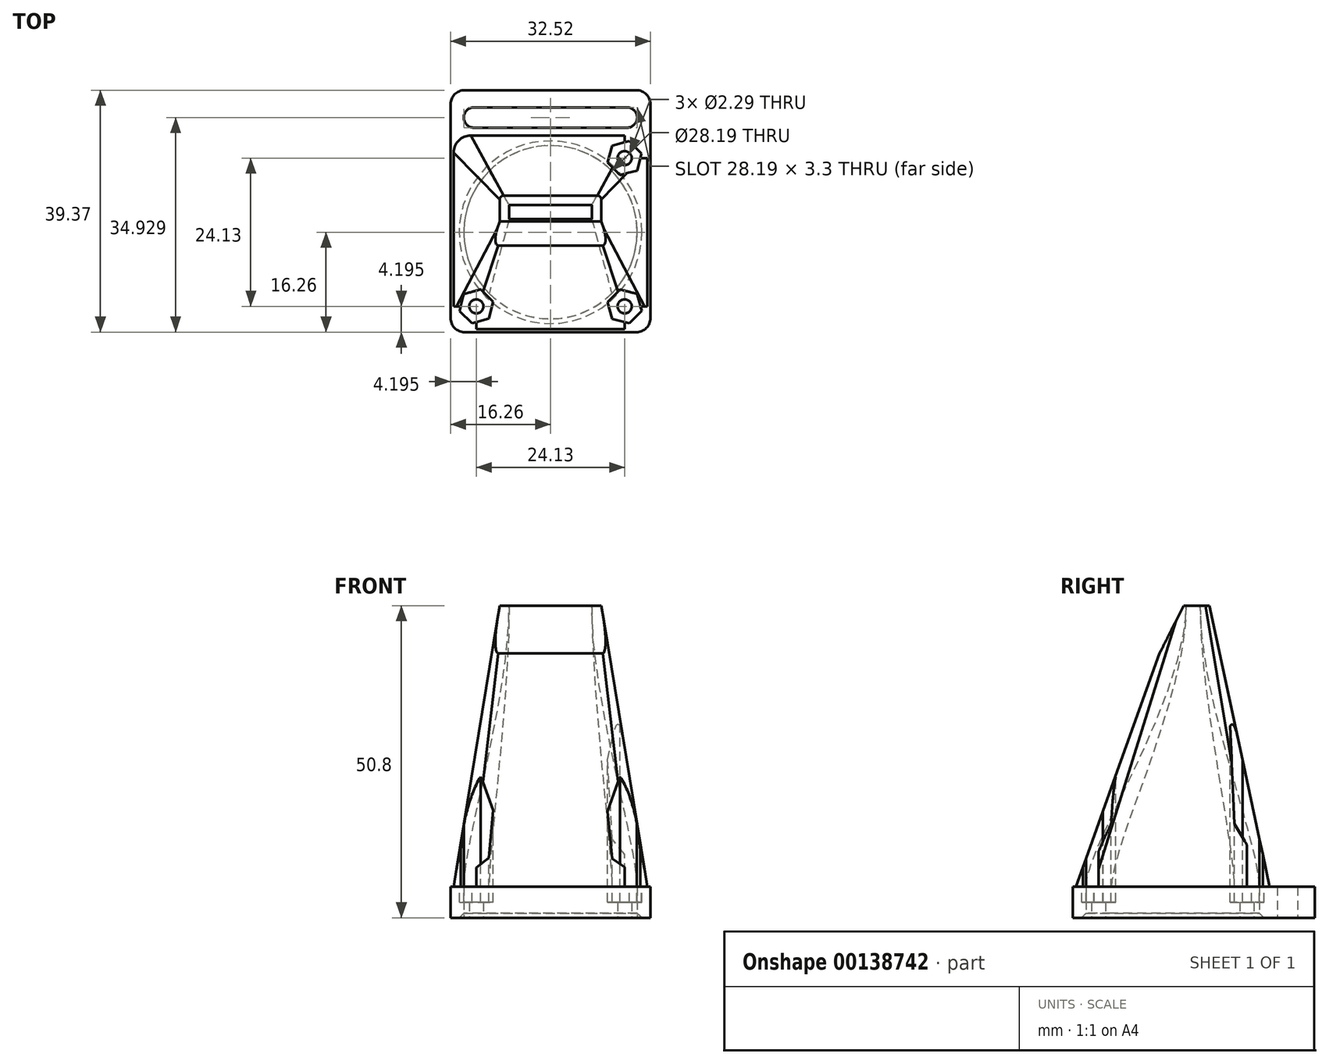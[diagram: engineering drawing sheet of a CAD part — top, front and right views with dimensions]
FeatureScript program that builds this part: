
annotation { "Feature Type Name" : "Feature", "Feature Type Description" : "" }
export const myFeature = defineFeature(function(context is Context, id is Id, definition is map)
    precondition{}
    {
        {
            var Q0;
            Q0=qCreatedBy(makeId("Top.planeOp"),FACE);
            var sketch = newSketch(context, id + "F0", { "sketchPlane" : qUnion([Q0])});
            skCircle(sketch, "E0", {"center": v(0, 0) * mm, "radius": 14.1 * mm});
            skLineSegment(sketch, "E1.top", {"start": v(-13.97, -16.26) * mm, "end": v(13.97, -16.26) * mm});
            skLineSegment(sketch, "E1.left", {"start": v(-16.26, 20.83) * mm, "end": v(-16.26, -13.97) * mm});
            skLineSegment(sketch, "E1.right", {"start": v(16.26, 20.83) * mm, "end": v(16.26, -13.97) * mm});
            skCircle(sketch, "E2", {"center": v(12.07, -12.07) * mm, "radius": 1.14 * mm});
            skCircle(sketch, "E3", {"center": v(-12.07, -12.07) * mm, "radius": 1.14 * mm});
            skCircle(sketch, "E4", {"center": v(12.07, 12.06) * mm, "radius": 1.14 * mm});
            skPoint(sketch, "E5.visualSharp", {"position": v(16.26, -16.26) * mm});
            skArc(sketch, "E5.filletArc", {"start": v(13.97, -16.26) * mm, "mid": v(15.59, -15.59) * mm, "end": v(16.26, -13.97) * mm});
            skPoint(sketch, "E6.visualSharp", {"position": v(-16.26, -16.26) * mm});
            skArc(sketch, "E6.filletArc", {"start": v(-16.26, -13.97) * mm, "mid": v(-15.59, -15.59) * mm, "end": v(-13.97, -16.26) * mm});
            skLineSegment(sketch, "E7.top", {"start": v(-13.97, 23.11) * mm, "end": v(13.97, 23.11) * mm});
            skArc(sketch, "E8", {"start": v(12.45, 17.02) * mm, "mid": v(14.1, 18.67) * mm, "end": v(12.45, 20.32) * mm});
            skArc(sketch, "E9", {"start": v(-12.45, 20.32) * mm, "mid": v(-14.1, 18.67) * mm, "end": v(-12.45, 17.02) * mm});
            skLineSegment(sketch, "E10", {"start": v(-12.45, 20.32) * mm, "end": v(12.45, 20.32) * mm});
            skLineSegment(sketch, "E11", {"start": v(12.45, 17.02) * mm, "end": v(-12.45, 17.02) * mm});
            skPoint(sketch, "E12.visualSharp", {"position": v(16.26, 23.11) * mm});
            skArc(sketch, "E12.filletArc", {"start": v(16.26, 20.83) * mm, "mid": v(15.59, 22.44) * mm, "end": v(13.97, 23.11) * mm});
            skPoint(sketch, "E13.visualSharp", {"position": v(-16.26, 23.11) * mm});
            skArc(sketch, "E13.filletArc", {"start": v(-13.97, 23.11) * mm, "mid": v(-15.59, 22.44) * mm, "end": v(-16.26, 20.83) * mm});
            skSolve(sketch);
        }
        {
            var Q0;
            Q0=qSketchRegion(id+"F0",true);
            extrude(context, id + "F1", {"entities" : qUnion([Q0]), "depth" : 5.08 * mm});
        }
        {
            var Q0;
            Q0=qCreatedBy(makeId("Top.planeOp"),FACE);
            cPlane(context, id + "F2", {"entities" : qUnion([Q0]), "cplaneType" : CPlaneType.OFFSET, "offset" : 50.8 * mm, "width" : 152.4 * mm, "height" : 152.4 * mm});
        }
        {
            var Q0;
            Q0=qCreatedBy(id+"F2.planeOp",FACE);
            var sketch = newSketch(context, id + "F3", { "sketchPlane" : qUnion([Q0])});
            skLineSegment(sketch, "E14.bottom", {"start": v(7.62, 0.63) * mm, "end": v(-7.62, 0.63) * mm});
            skLineSegment(sketch, "E14.top", {"start": v(7.62, 5.97) * mm, "end": v(-7.62, 5.97) * mm});
            skLineSegment(sketch, "E14.left", {"start": v(8.26, 1.27) * mm, "end": v(8.26, 5.33) * mm});
            skLineSegment(sketch, "E14.right", {"start": v(-8.26, 1.27) * mm, "end": v(-8.26, 5.33) * mm});
            skPoint(sketch, "E14.middle", {"position": v(0, 3.3) * mm});
            skPoint(sketch, "E15.visualSharp", {"position": v(-8.26, 5.97) * mm});
            skArc(sketch, "E15.filletArc", {"start": v(-7.62, 5.97) * mm, "mid": v(-8.07, 5.78) * mm, "end": v(-8.26, 5.33) * mm});
            skPoint(sketch, "E16.visualSharp", {"position": v(8.26, 5.97) * mm});
            skArc(sketch, "E16.filletArc", {"start": v(8.26, 5.33) * mm, "mid": v(8.07, 5.78) * mm, "end": v(7.62, 5.97) * mm});
            skPoint(sketch, "E17.visualSharp", {"position": v(8.26, 0.63) * mm});
            skArc(sketch, "E17.filletArc", {"start": v(7.62, 0.63) * mm, "mid": v(8.07, 0.82) * mm, "end": v(8.26, 1.27) * mm});
            skPoint(sketch, "E18.visualSharp", {"position": v(-8.26, 0.63) * mm});
            skArc(sketch, "E18.filletArc", {"start": v(-8.26, 1.27) * mm, "mid": v(-8.07, 0.82) * mm, "end": v(-7.62, 0.63) * mm});
            skSolve(sketch);
        }
        {
            var Q0;
            Q0=makeQuery(id+"F1.opExtrude","CAP_FACE",FACE,{"disambiguationData":[OSD([sQuery(id+"F0.wireOp",EDGE,"E0"),sQuery(id+"F0.wireOp",EDGE,"E1.bottom"),sQuery(id+"F0.wireOp",EDGE,"E1.top"),sQuery(id+"F0.wireOp",EDGE,"E1.left"),sQuery(id+"F0.wireOp",EDGE,"E1.right"),sQuery(id+"F0.wireOp",EDGE,"E2"),sQuery(id+"F0.wireOp",EDGE,"E3"),sQuery(id+"F0.wireOp",EDGE,"E4"),sQuery(id+"F0.wireOp",EDGE,"E5.filletArc"),sQuery(id+"F0.wireOp",EDGE,"E6.filletArc"),sQuery(id+"F0.wireOp",EDGE,"149f5cb3-4573-49cd-96a3-69cfe59d07a0"),sQuery(id+"F0.wireOp",EDGE,"d382702d-8765-46b1-bb4a-e5bcc725e8f2"),sQuery(id+"F0.wireOp",EDGE,"7psakdMX-4Kjn-pSWq-Gzre-Dv3dCUeNbaRH"),sQuery(id+"F0.wireOp",EDGE,"2zvfWlE9-K41b-0TAf-VtaE-B6S3niEw6Jqb"),sQuery(id+"F0.wireOp",EDGE,"dzUK1zkA-kHCU-L9Y5-sRFk-Q5gVuIE2vdbO"),sQuery(id+"F0.wireOp",EDGE,"SnxPUKdg-JB6R-aEuo-4lix-42RaE0Bb72ui"),sQuery(id+"F0.wireOp",EDGE,"qkKqWLcb-ILKv-onpQ-n0cg-Ra0XMfHJsXs8"),sQuery(id+"F0.wireOp",EDGE,"7cRavyST-Wl7Z-z6MU-cKR1-3YkR6QLB8JKU")])],"isStart":false});
            var sketch = newSketch(context, id + "F4", { "sketchPlane" : qUnion([Q0])});
            skLineSegment(sketch, "E19.bottom", {"start": v(12.95, 15.75) * mm, "end": v(-12.95, 15.75) * mm});
            skLineSegment(sketch, "E19.top", {"start": v(12.95, -15.75) * mm, "end": v(-12.95, -15.75) * mm});
            skLineSegment(sketch, "E19.left", {"start": v(15.75, 12.95) * mm, "end": v(15.75, -12.95) * mm});
            skLineSegment(sketch, "E19.right", {"start": v(-15.75, 12.95) * mm, "end": v(-15.75, -12.95) * mm});
            skCircle(sketch, "E20", {"center": v(0, 0) * mm, "radius": 14.22 * mm, "construction": true});
            skPoint(sketch, "E21.visualSharp", {"position": v(-15.75, -15.75) * mm});
            skArc(sketch, "E21.filletArc", {"start": v(-15.75, -12.95) * mm, "mid": v(-14.93, -14.93) * mm, "end": v(-12.95, -15.75) * mm});
            skPoint(sketch, "E22.visualSharp", {"position": v(15.75, -15.75) * mm});
            skArc(sketch, "E22.filletArc", {"start": v(12.95, -15.75) * mm, "mid": v(14.93, -14.93) * mm, "end": v(15.75, -12.95) * mm});
            skPoint(sketch, "E23.visualSharp", {"position": v(15.75, 15.75) * mm});
            skArc(sketch, "E23.filletArc", {"start": v(15.75, 12.95) * mm, "mid": v(14.93, 14.93) * mm, "end": v(12.95, 15.75) * mm});
            skPoint(sketch, "E24.visualSharp", {"position": v(-15.75, 15.75) * mm});
            skArc(sketch, "E24.filletArc", {"start": v(-12.95, 15.75) * mm, "mid": v(-14.93, 14.93) * mm, "end": v(-15.75, 12.95) * mm});
            skSolve(sketch);
        }
        {
            var Q1;
            Q1=qSketchRegion(id+"F3",true);
            var Q2;
            Q2=qSketchRegion(id+"F4",true);
            loft(context, id + "F5", {"operationType" : NewBodyOperationType.ADD, "sheetProfilesArray" : [{ "sheetProfileEntities" : qUnion([Q1]) }, { "sheetProfileEntities" : qUnion([Q2]) }]});
        }
        {
            var Q0;
            Q0=qCreatedBy(id+"F2.planeOp",FACE);
            var sketch = newSketch(context, id + "F6", { "sketchPlane" : qUnion([Q0])});
            skCircle(sketch, "E25.cCircle", {"center": v(-12.07, -12.07) * mm, "radius": 2.48 * mm, "construction": true});
            skLineSegment(sketch, "E25.0", {"start": v(-9.31, -11.3) * mm, "end": v(-10.02, -14.06) * mm});
            skLineSegment(sketch, "E25.1", {"start": v(-10.02, -14.06) * mm, "end": v(-12.77, -14.84) * mm});
            skLineSegment(sketch, "E25.2", {"start": v(-12.77, -14.84) * mm, "end": v(-14.82, -12.84) * mm});
            skLineSegment(sketch, "E25.3", {"start": v(-14.82, -12.84) * mm, "end": v(-14.1, -10.07) * mm});
            skLineSegment(sketch, "E25.4", {"start": v(-14.1, -10.07) * mm, "end": v(-11.36, -9.3) * mm});
            skLineSegment(sketch, "E25.5", {"start": v(-11.36, -9.3) * mm, "end": v(-9.31, -11.3) * mm});
            skPoint(sketch, "E25.0.midPoint", {"position": v(-9.67, -12.68) * mm});
            skCircle(sketch, "E26.cCircle", {"center": v(12.07, -12.07) * mm, "radius": 2.48 * mm, "construction": true});
            skLineSegment(sketch, "E26.0", {"start": v(12.84, -14.82) * mm, "end": v(10.07, -14.11) * mm});
            skLineSegment(sketch, "E26.1", {"start": v(10.07, -14.11) * mm, "end": v(9.3, -11.36) * mm});
            skLineSegment(sketch, "E26.2", {"start": v(9.3, -11.36) * mm, "end": v(11.29, -9.31) * mm});
            skLineSegment(sketch, "E26.3", {"start": v(11.29, -9.31) * mm, "end": v(14.06, -10.02) * mm});
            skLineSegment(sketch, "E26.4", {"start": v(14.06, -10.02) * mm, "end": v(14.84, -12.77) * mm});
            skLineSegment(sketch, "E26.5", {"start": v(14.84, -12.77) * mm, "end": v(12.84, -14.82) * mm});
            skPoint(sketch, "E26.0.midPoint", {"position": v(11.46, -14.47) * mm});
            skCircle(sketch, "E27.cCircle", {"center": v(12.07, 12.06) * mm, "radius": 2.48 * mm, "construction": true});
            skLineSegment(sketch, "E27.0", {"start": v(14.07, 10.03) * mm, "end": v(11.3, 9.3) * mm});
            skLineSegment(sketch, "E27.1", {"start": v(11.3, 9.3) * mm, "end": v(9.3, 11.34) * mm});
            skLineSegment(sketch, "E27.2", {"start": v(9.3, 11.34) * mm, "end": v(10.06, 14.1) * mm});
            skLineSegment(sketch, "E27.3", {"start": v(10.06, 14.1) * mm, "end": v(12.82, 14.82) * mm});
            skLineSegment(sketch, "E27.4", {"start": v(12.82, 14.82) * mm, "end": v(14.83, 12.79) * mm});
            skLineSegment(sketch, "E27.5", {"start": v(14.83, 12.79) * mm, "end": v(14.07, 10.03) * mm});
            skPoint(sketch, "E27.0.midPoint", {"position": v(12.7, 9.67) * mm});
            skSolve(sketch);
        }
        {
            var Q0;
            Q0=qSketchRegion(id+"F6",true);
            extrude(context, id + "F7", {"entities" : qUnion([Q0]), "operationType" : NewBodyOperationType.REMOVE, "oppositeDirection" : true, "depth" : 48.26 * mm});
        }
        {
            var Q0;
            Q0=qCreatedBy(id+"F2.planeOp",FACE);
            var sketch = newSketch(context, id + "F8", { "sketchPlane" : qUnion([Q0])});
            skLineSegment(sketch, "E28.bottom", {"start": v(6.73, 2.16) * mm, "end": v(-6.73, 2.16) * mm});
            skLineSegment(sketch, "E28.top", {"start": v(6.73, 4.44) * mm, "end": v(-6.73, 4.44) * mm});
            skLineSegment(sketch, "E28.left", {"start": v(6.73, 2.16) * mm, "end": v(6.73, 4.44) * mm});
            skLineSegment(sketch, "E28.right", {"start": v(-6.73, 2.16) * mm, "end": v(-6.73, 4.44) * mm});
            skSolve(sketch);
        }
        {
            var Q0;
            Q0=makeQuery(id+"F1.opExtrude","CAP_FACE",FACE,{"disambiguationData":[OSD([sQuery(id+"F0.wireOp",EDGE,"E0"),sQuery(id+"F0.wireOp",EDGE,"E1.bottom"),sQuery(id+"F0.wireOp",EDGE,"E1.top"),sQuery(id+"F0.wireOp",EDGE,"E1.left"),sQuery(id+"F0.wireOp",EDGE,"E1.right"),sQuery(id+"F0.wireOp",EDGE,"E2"),sQuery(id+"F0.wireOp",EDGE,"E3"),sQuery(id+"F0.wireOp",EDGE,"E4"),sQuery(id+"F0.wireOp",EDGE,"E5.filletArc"),sQuery(id+"F0.wireOp",EDGE,"E6.filletArc"),sQuery(id+"F0.wireOp",EDGE,"149f5cb3-4573-49cd-96a3-69cfe59d07a0"),sQuery(id+"F0.wireOp",EDGE,"d382702d-8765-46b1-bb4a-e5bcc725e8f2"),sQuery(id+"F0.wireOp",EDGE,"7psakdMX-4Kjn-pSWq-Gzre-Dv3dCUeNbaRH"),sQuery(id+"F0.wireOp",EDGE,"2zvfWlE9-K41b-0TAf-VtaE-B6S3niEw6Jqb"),sQuery(id+"F0.wireOp",EDGE,"dzUK1zkA-kHCU-L9Y5-sRFk-Q5gVuIE2vdbO"),sQuery(id+"F0.wireOp",EDGE,"SnxPUKdg-JB6R-aEuo-4lix-42RaE0Bb72ui"),sQuery(id+"F0.wireOp",EDGE,"qkKqWLcb-ILKv-onpQ-n0cg-Ra0XMfHJsXs8"),sQuery(id+"F0.wireOp",EDGE,"7cRavyST-Wl7Z-z6MU-cKR1-3YkR6QLB8JKU")])],"isStart":false});
            var sketch = newSketch(context, id + "F9", { "sketchPlane" : qUnion([Q0])});
            skCircle(sketch, "E29", {"center": v(0, 0) * mm, "radius": 14.1 * mm});
            skLineSegment(sketch, "E30", {"start": v(0, 0) * mm, "end": v(0, 6.97) * mm, "construction": true});
            skLineSegment(sketch, "E31", {"start": v(0, 0) * mm, "end": v(9.97, 9.97) * mm, "construction": true});
            skSolve(sketch);
        }
        {
            var Q1;
            Q1=qSketchRegion(id+"F8",true);
            var Q2;
            Q2=qSketchRegion(id+"F9",true);
            var Q3;
            Q3=sQuery(id+"F9.wireOp",VERTEX,"E31.end");
            var Q4;
            Q4=sQuery(id+"F8.wireOp",VERTEX,"E28.left.end");
            loft(context, id + "F10", {"operationType" : NewBodyOperationType.REMOVE, "startCondition" : LoftEndDerivativeType.NORMAL_TO_PROFILE, "startMagnitude" : 1, "endCondition" : LoftEndDerivativeType.NORMAL_TO_PROFILE, "endMagnitude" : .45, "sheetProfilesArray" : [{ "sheetProfileEntities" : qUnion([Q1]) }, { "sheetProfileEntities" : qUnion([Q2]) }], "matchConnections" : true, "connections" : [{ "connectionEntities" : qUnion([Q3, Q4]), "connectionEdgeQueries" : qUnion([]), "connectionEdgeParameters" : [] }]});
        }
        {
            var Q0;
            Q0=qCreatedBy(id+"F2.planeOp",FACE);
            var sketch = newSketch(context, id + "F11", { "sketchPlane" : qUnion([Q0])});
            skLineSegment(sketch, "E32.bottom", {"start": v(12.07, -12.07) * mm, "end": v(15.88, -12.07) * mm});
            skLineSegment(sketch, "E32.top", {"start": v(12.07, -15.88) * mm, "end": v(15.88, -15.88) * mm});
            skLineSegment(sketch, "E32.left", {"start": v(12.07, -12.07) * mm, "end": v(12.07, -15.88) * mm});
            skLineSegment(sketch, "E32.right", {"start": v(15.88, -12.07) * mm, "end": v(15.88, -15.88) * mm});
            skLineSegment(sketch, "E33.bottom", {"start": v(-12.07, -12.07) * mm, "end": v(-15.88, -12.07) * mm});
            skLineSegment(sketch, "E33.top", {"start": v(-12.07, -15.88) * mm, "end": v(-15.88, -15.88) * mm});
            skLineSegment(sketch, "E33.left", {"start": v(-12.07, -12.07) * mm, "end": v(-12.07, -15.88) * mm});
            skLineSegment(sketch, "E33.right", {"start": v(-15.88, -12.07) * mm, "end": v(-15.88, -15.88) * mm});
            skLineSegment(sketch, "E34.bottom", {"start": v(12.07, 12.06) * mm, "end": v(15.88, 12.06) * mm});
            skLineSegment(sketch, "E34.top", {"start": v(12.07, 15.88) * mm, "end": v(15.88, 15.88) * mm});
            skLineSegment(sketch, "E34.left", {"start": v(12.07, 12.06) * mm, "end": v(12.07, 15.88) * mm});
            skLineSegment(sketch, "E34.right", {"start": v(15.88, 12.06) * mm, "end": v(15.88, 15.88) * mm});
            skSolve(sketch);
        }
        {
            var Q0;
            Q0 = qSketchRegion(id + "F11", true);
            extrude(context, id + "F12", {"entities" : qUnion([Q0]), "operationType" : NewBodyOperationType.REMOVE, "oppositeDirection" : true, "depth" : 45.72 * mm});
        }
        {
            var Q0;
            Q0=qCreatedBy(makeId("Right.planeOp"),FACE);
            var sketch = newSketch(context, id + "F13", { "sketchPlane" : qUnion([Q0])});
            skLineSegment(sketch, "E35", {"start": v(1.9, 51.07) * mm, "end": v(-2.6, 42.15) * mm});
            skLineSegment(sketch, "E36", {"start": v(-2.6, 42.15) * mm, "end": v(-2.6, 51.07) * mm});
            skLineSegment(sketch, "E37", {"start": v(-2.6, 51.07) * mm, "end": v(1.9, 51.07) * mm});
            skSolve(sketch);
        }
        {
            var Q0;
            Q0 = qSketchRegion(id + "F13", true);
            extrude(context, id + "F14", {"entities" : qUnion([Q0]), "operationType" : NewBodyOperationType.REMOVE, "endBound" : BoundingType.SYMMETRIC, "oppositeDirection" : true, "depth" : 25.4 * mm});
        }
        {
            var Q0;
            Q0=makeQuery(id+"F1.opExtrude","CAP_EDGE",EDGE,{"disambiguationData":[OSD([sQuery(id+"F0.wireOp",EDGE,"E0")])],"isStart":true});
            chamfer(context, id + "F15", {"entities" : qUnion([Q0]), "width" : 0.76 * mm, "tangentPropagation" : true});
        }
    });
